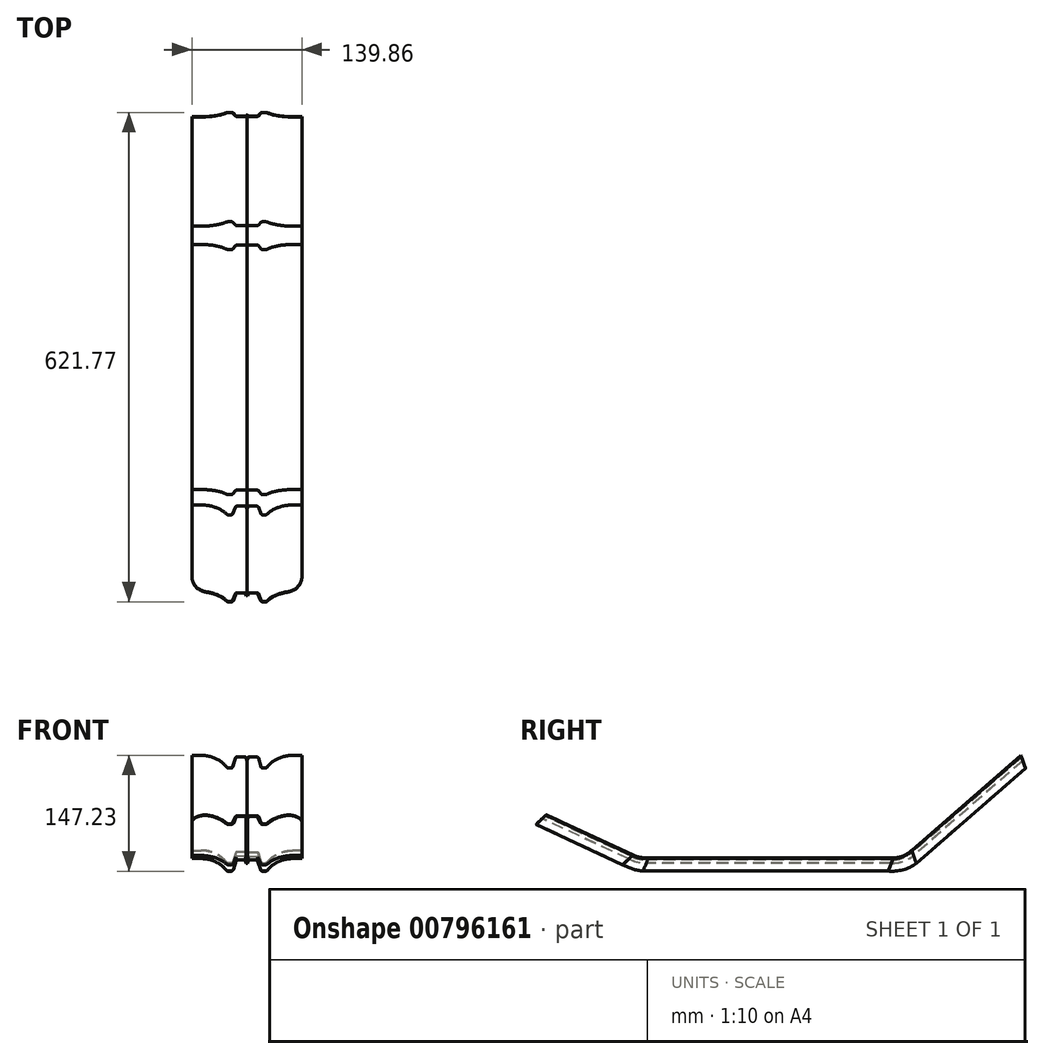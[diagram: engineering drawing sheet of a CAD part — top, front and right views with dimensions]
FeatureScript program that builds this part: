
annotation { "Feature Type Name" : "Feature", "Feature Type Description" : "" }
export const myFeature = defineFeature(function(context is Context, id is Id, definition is map)
    precondition{}
    {
        {
            var Q0;
            Q0=qCreatedBy(makeId("Front.planeOp"),FACE);
            var sketch = newSketch(context, id + "F0", { "sketchPlane" : qUnion([Q0])});
            skLineSegment(sketch, "E0", {"start": v(0, 0) * mm, "end": v(-1.14, 3.6) * mm});
            skLineSegment(sketch, "E1", {"start": v(-3.05, 5) * mm, "end": v(-12.59, 5) * mm});
            skLineSegment(sketch, "E2", {"start": v(-14.5, 3.55) * mm, "end": v(-17.99, -8.55) * mm});
            skLineSegment(sketch, "E3", {"start": v(-19.91, -10) * mm, "end": v(-23.8, -10) * mm});
            skLineSegment(sketch, "E4", {"start": v(0, 0) * mm, "end": v(-70, 0) * mm, "construction": true});
            skLineSegment(sketch, "E5", {"start": v(-7.84, 5) * mm, "end": v(-7.84, 7) * mm, "construction": true});
            skLineSegment(sketch, "E6", {"start": v(-69.93, 7) * mm, "end": v(-57.93, 7) * mm});
            skArc(sketch, "E7", {"start": v(-25.4, -9.2) * mm, "mid": v(-39.75, 2.72) * mm, "end": v(-57.93, 7) * mm});
            skPoint(sketch, "E8.visualSharp", {"position": v(-14.1, 5) * mm});
            skArc(sketch, "E8.filletArc", {"start": v(-12.59, 5) * mm, "mid": v(-13.79, 4.6) * mm, "end": v(-14.5, 3.55) * mm});
            skPoint(sketch, "E9.visualSharp", {"position": v(-1.58, 5) * mm});
            skArc(sketch, "E9.filletArc", {"start": v(-1.14, 3.6) * mm, "mid": v(-1.87, 4.61) * mm, "end": v(-3.05, 5) * mm});
            skPoint(sketch, "E10.visualSharp", {"position": v(-18.4, -10) * mm});
            skArc(sketch, "E10.filletArc", {"start": v(-19.91, -10) * mm, "mid": v(-18.7, -9.6) * mm, "end": v(-17.99, -8.55) * mm});
            skPoint(sketch, "E11.visualSharp", {"position": v(-24.8, -10) * mm});
            skArc(sketch, "E11.filletArc", {"start": v(-25.4, -9.2) * mm, "mid": v(-24.69, -9.8) * mm, "end": v(-23.8, -10) * mm});
            skLineSegment(sketch, "E12.0", {"start": v(-0.76, -0.24) * mm, "end": v(-1.9, 3.36) * mm});
            skArc(sketch, "E12.1", {"start": v(-1.9, 3.36) * mm, "mid": v(-2.34, 3.97) * mm, "end": v(-3.05, 4.2) * mm});
            skLineSegment(sketch, "E12.2", {"start": v(-3.05, 4.2) * mm, "end": v(-12.59, 4.2) * mm});
            skArc(sketch, "E12.3", {"start": v(-12.59, 4.2) * mm, "mid": v(-13.3, 3.96) * mm, "end": v(-13.74, 3.33) * mm});
            skLineSegment(sketch, "E12.4", {"start": v(-13.74, 3.33) * mm, "end": v(-17.22, -8.77) * mm});
            skArc(sketch, "E12.5", {"start": v(-19.91, -10.8) * mm, "mid": v(-18.23, -10.24) * mm, "end": v(-17.22, -8.77) * mm});
            skLineSegment(sketch, "E12.6", {"start": v(-69.93, 6.2) * mm, "end": v(-57.93, 6.2) * mm});
            skArc(sketch, "E12.7", {"start": v(-26.03, -9.69) * mm, "mid": v(-40.11, 2) * mm, "end": v(-57.93, 6.2) * mm});
            skArc(sketch, "E12.8", {"start": v(-26.03, -9.69) * mm, "mid": v(-25.04, -10.5) * mm, "end": v(-23.8, -10.8) * mm});
            skLineSegment(sketch, "E12.9", {"start": v(-19.91, -10.8) * mm, "end": v(-23.8, -10.8) * mm});
            skLineSegment(sketch, "E13", {"start": v(-0.76, -0.24) * mm, "end": v(0, 0) * mm});
            skLineSegment(sketch, "E14", {"start": v(-69.93, 7) * mm, "end": v(-69.93, 6.2) * mm});
            skSolve(sketch);
        }
        {
            var Q0;
            Q0=qCreatedBy(makeId("Right.planeOp"),FACE);
            var sketch = newSketch(context, id + "F1", { "sketchPlane" : qUnion([Q0])});
            skLineSegment(sketch, "E15", {"start": v(-14.96, 0) * mm, "end": v(-326.2, 0) * mm});
            skLineSegment(sketch, "E16", {"start": v(-347.34, 4.68) * mm, "end": v(-457.3, 55.96) * mm});
            skPoint(sketch, "E17.visualSharp", {"position": v(-337.3, 0) * mm});
            skArc(sketch, "E17.filletArc", {"start": v(-347.34, 4.68) * mm, "mid": v(-337.03, 1.19) * mm, "end": v(-326.2, 0) * mm});
            skLineSegment(sketch, "E18", {"start": v(11.29, 9.81) * mm, "end": v(150, 130.4) * mm});
            skPoint(sketch, "E19.visualSharp", {"position": v(0, 0) * mm});
            skArc(sketch, "E19.filletArc", {"start": v(-14.96, 0) * mm, "mid": v(-0.95, 2.53) * mm, "end": v(11.29, 9.81) * mm});
            skSolve(sketch);
        }
        {
            var Q0;
            Q0=makeQuery(id+"F0.imprint","IMPRINT",FACE,{"disambiguationData":[TD([[makeQuery(id+"F0.imprint","IMPRINT",EDGE,{"derivedFrom":sQuery(id+"F0.wireOp",EDGE,"E0")}),1.0]])]});
            var Q1;
            Q1=sQuery(id+"F1.wireOp",EDGE,"E15");
            var Q2;
            Q2=sQuery(id+"F1.wireOp",EDGE,"E17.filletArc");
            var Q3;
            Q3=sQuery(id+"F1.wireOp",EDGE,"E16");
            var Q4;
            Q4=sQuery(id+"F1.wireOp",EDGE,"E19.filletArc");
            var Q5;
            Q5=sQuery(id+"F1.wireOp",EDGE,"E18");
            sweep(context, id + "F2", {"profiles" : qUnion([Q0]), "path" : qUnion([Q1, Q2, Q3, Q4, Q5])});
        }
        {
            var Q0;
            Q0=makeQuery(id+"F2.opSweep","CAP_EDGE",EDGE,{"disambiguationData":[OSD([sQuery(id+"F0.wireOp",EDGE,"E14"),sQuery(id+"F1.wireOp",VERTEX,"E16.end")])],"isStart":false});
            fillet(context, id + "F3", {"entities" : qUnion([Q0]), "radius" : 20 * mm, "tangentPropagation" : true, "allowEdgeOverflow" : false});
        }
        {
            var Q0;
            Q0=makeQuery(id+"F2.opSweep","SWEPT_BODY",BODY,{"disambiguationData":[OSD([sQuery(id+"F0.wireOp",EDGE,"E0"),sQuery(id+"F0.wireOp",EDGE,"E1"),sQuery(id+"F0.wireOp",EDGE,"E2"),sQuery(id+"F0.wireOp",EDGE,"E3"),sQuery(id+"F0.wireOp",EDGE,"E6"),sQuery(id+"F0.wireOp",EDGE,"E7"),sQuery(id+"F0.wireOp",EDGE,"E8.filletArc"),sQuery(id+"F0.wireOp",EDGE,"E9.filletArc"),sQuery(id+"F0.wireOp",EDGE,"E10.filletArc"),sQuery(id+"F0.wireOp",EDGE,"E11.filletArc"),sQuery(id+"F0.wireOp",EDGE,"E12.0"),sQuery(id+"F0.wireOp",EDGE,"E12.1"),sQuery(id+"F0.wireOp",EDGE,"E12.2"),sQuery(id+"F0.wireOp",EDGE,"E12.3"),sQuery(id+"F0.wireOp",EDGE,"E12.4"),sQuery(id+"F0.wireOp",EDGE,"E12.5"),sQuery(id+"F0.wireOp",EDGE,"E12.6"),sQuery(id+"F0.wireOp",EDGE,"E12.7"),sQuery(id+"F0.wireOp",EDGE,"E12.8"),sQuery(id+"F0.wireOp",EDGE,"E12.9"),sQuery(id+"F0.wireOp",EDGE,"E13"),sQuery(id+"F0.wireOp",EDGE,"E14"),sQuery(id+"F1.wireOp",EDGE,"E16")])]});
            var Q1;
            Q1=qCreatedBy(makeId("Right.planeOp"),FACE);
            mirror(context, id + "F4", {"operationType" : NewBodyOperationType.ADD, "entities" : qUnion([Q0]), "mirrorPlane" : qUnion([Q1])});
        }
    });
